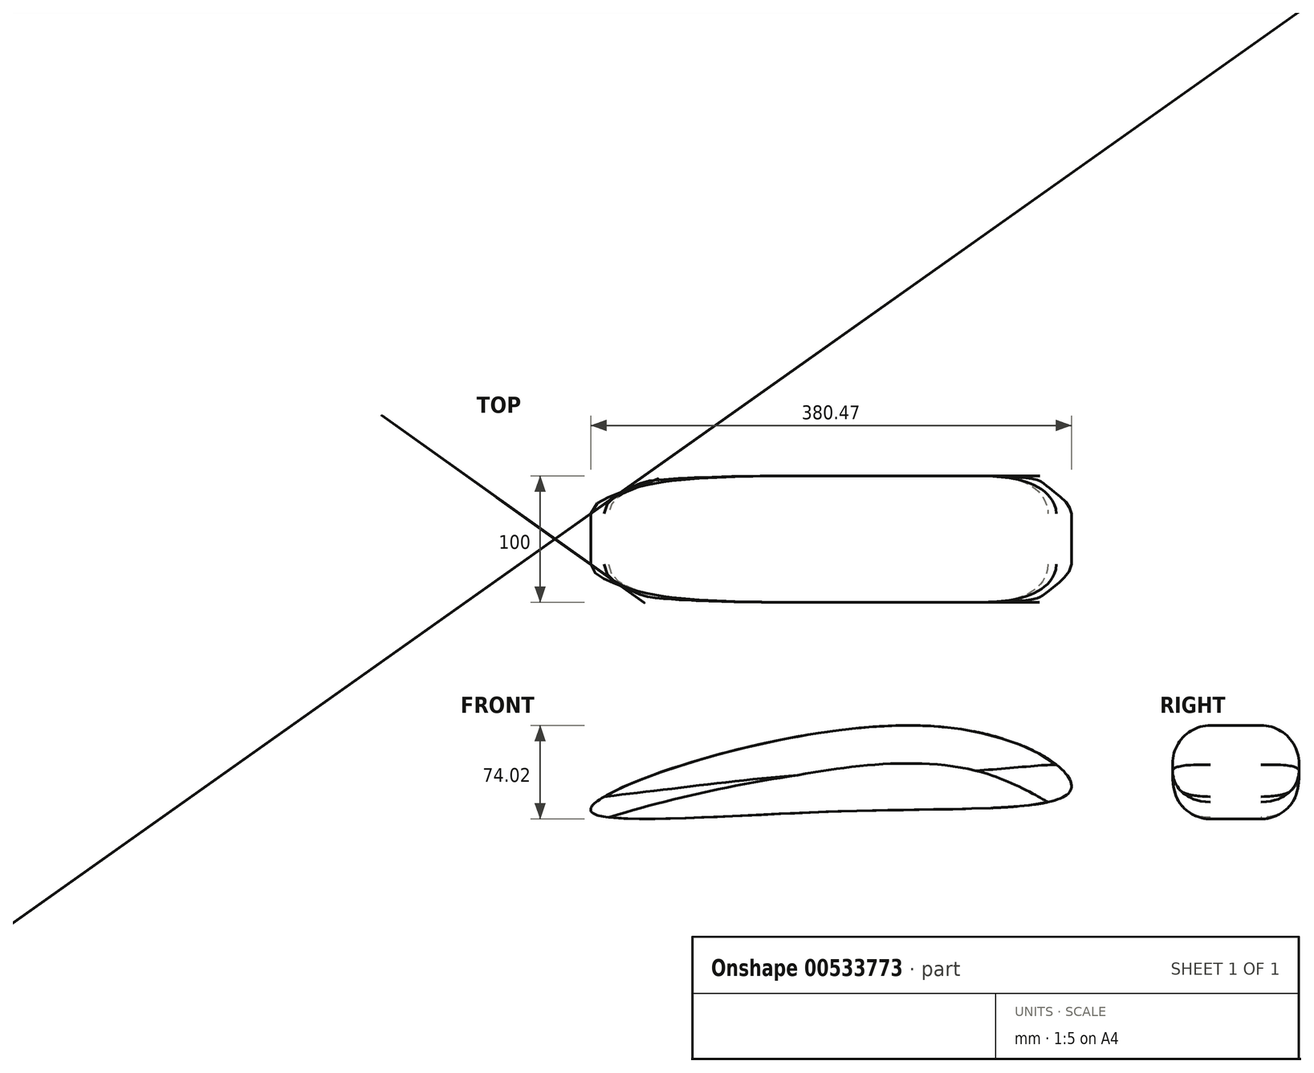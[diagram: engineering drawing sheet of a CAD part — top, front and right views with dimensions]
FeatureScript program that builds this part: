
annotation { "Feature Type Name" : "Feature", "Feature Type Description" : "" }
export const myFeature = defineFeature(function(context is Context, id is Id, definition is map)
    precondition{}
    {
        {
            var Q0;
            Q0=qCreatedBy(makeId("Front.planeOp"),FACE);
            var sketch = newSketch(context, id + "F0", { "sketchPlane" : qUnion([Q0])});
            skFitSpline(sketch, "E0.0.0", {"points": [v(113.35, 23.22) * mm, v(113.44, 23.66) * mm, v(113.5, 24.56) * mm, v(113.2, 25.94) * mm, v(112.62, 27.29) * mm, v(111.79, 28.58) * mm, v(110.78, 29.82) * mm, v(109.65, 31) * mm, v(108.43, 32.12) * mm, v(106.71, 33.54) * mm, v(104.45, 35.18) * mm, v(101.68, 36.95) * mm, v(99.37, 38.26) * mm, v(97.55, 39.22) * mm, v(96.2, 39.89) * mm, v(94.85, 40.52) * mm, v(93.51, 41.11) * mm, v(92.17, 41.68) * mm, v(90.82, 42.23) * mm, v(89.45, 42.77) * mm, v(87.6, 43.47) * mm, v(85.24, 44.34) * mm, v(82.34, 45.37) * mm, v(79.4, 46.38) * mm, v(76.43, 47.36) * mm, v(73.46, 48.29) * mm, v(70.5, 49.16) * mm, v(67.54, 49.97) * mm, v(64.6, 50.72) * mm, v(61.64, 51.42) * mm, v(58.66, 52.07) * mm, v(54.68, 52.9) * mm, v(49.65, 53.84) * mm, v(43.57, 54.8) * mm, v(37.48, 55.61) * mm, v(31.4, 56.27) * mm, v(25.3, 56.82) * mm, v(19.19, 57.28) * mm, v(11.02, 57.8) * mm, v(2.86, 58.15) * mm, v(-5.3, 58.39) * mm, v(-11.44, 58.5) * mm, v(-17.57, 58.56) * mm, v(-23.7, 58.55) * mm, v(-29.82, 58.49) * mm, v(-38, 58.32) * mm, v(-48.2, 57.99) * mm, v(-58.4, 57.48) * mm, v(-66.56, 56.97) * mm, v(-72.68, 56.54) * mm, v(-78.79, 56.06) * mm, v(-86.93, 55.36) * mm, v(-97.1, 54.37) * mm, v(-107.24, 53.24) * mm, v(-115.35, 52.25) * mm, v(-121.43, 51.47) * mm, v(-127.5, 50.65) * mm, v(-135.58, 49.5) * mm, v(-145.64, 48) * mm, v(-155.68, 46.37) * mm, v(-163.73, 45) * mm, v(-169.76, 43.94) * mm, v(-175.8, 42.85) * mm, v(-181.8, 41.74) * mm, v(-187.8, 40.6) * mm, v(-192.81, 39.62) * mm, v(-196.82, 38.82) * mm, v(-200.83, 38.02) * mm, v(-207.85, 36.6) * mm, v(-214.87, 35.12) * mm, v(-220.87, 33.83) * mm, v(-223.86, 33.18) * mm, v(-226.86, 32.52) * mm, v(-229.87, 31.85) * mm, v(-232.9, 31.17) * mm, v(-235.92, 30.5) * mm, v(-238.94, 29.8) * mm, v(-241.93, 29.11) * mm, v(-244.91, 28.42) * mm, v(-247.9, 27.71) * mm, v(-250.86, 27) * mm, v(-254.8, 26.03) * mm, v(-259.73, 24.78) * mm, v(-263.68, 23.75) * mm, v(-265.65, 23.22) * mm]});
            skFitSpline(sketch, "E0.0.1", {"points": [v(-265.65, 23.22) * mm, v(-263.64, 23.1) * mm, v(-259.61, 22.89) * mm, v(-253.56, 22.6) * mm, v(-247.58, 22.34) * mm, v(-241.63, 22.12) * mm, v(-235.63, 21.9) * mm, v(-229.58, 21.7) * mm, v(-223.53, 21.5) * mm, v(-217.48, 21.29) * mm, v(-212.44, 21.12) * mm, v(-208.4, 20.98) * mm, v(-205.38, 20.88) * mm, v(-202.36, 20.78) * mm, v(-199.38, 20.68) * mm, v(-196.47, 20.58) * mm, v(-193.64, 20.48) * mm, v(-190.86, 20.39) * mm, v(-187.22, 20.26) * mm, v(-183.62, 20.14) * mm, v(-179.94, 20.01) * mm, v(-177.12, 19.92) * mm, v(-174.23, 19.82) * mm, v(-171.27, 19.71) * mm, v(-168.76, 19.63) * mm, v(-166.74, 19.56) * mm, v(-164.73, 19.49) * mm, v(-162.2, 19.4) * mm, v(-158.17, 19.26) * mm, v(-153.13, 19.09) * mm, v(-147.08, 18.88) * mm, v(-142.04, 18.7) * mm, v(-138, 18.56) * mm, v(-134.98, 18.46) * mm, v(-131.96, 18.35) * mm, v(-128.93, 18.25) * mm, v(-125.9, 18.15) * mm, v(-122.95, 18.04) * mm, v(-120.08, 17.94) * mm, v(-117.3, 17.85) * mm, v(-114.6, 17.76) * mm, v(-111.07, 17.63) * mm, v(-107.59, 17.51) * mm, v(-104.02, 17.4) * mm, v(-101.27, 17.3) * mm, v(-98.44, 17.2) * mm, v(-95.51, 17.1) * mm, v(-93.01, 17.01) * mm, v(-91, 16.94) * mm, v(-88.98, 16.87) * mm, v(-86.46, 16.78) * mm, v(-82.42, 16.64) * mm, v(-77.38, 16.47) * mm, v(-71.33, 16.26) * mm, v(-63.27, 15.98) * mm, v(-53.18, 15.63) * mm, v(-41.08, 15.2) * mm, v(-28.98, 14.79) * mm, v(-16.88, 14.37) * mm, v(-4.78, 13.94) * mm, v(5.3, 13.6) * mm, v(13.37, 13.33) * mm, v(19.42, 13.14) * mm, v(25.47, 12.95) * mm, v(31.5, 12.78) * mm, v(36.53, 12.67) * mm, v(40.57, 12.6) * mm, v(43.6, 12.56) * mm, v(46.65, 12.52) * mm, v(49.68, 12.5) * mm, v(52.71, 12.47) * mm, v(55.72, 12.45) * mm, v(58.73, 12.44) * mm, v(61.73, 12.45) * mm, v(64.75, 12.48) * mm, v(67.78, 12.54) * mm, v(70.84, 12.64) * mm, v(73.92, 12.77) * mm, v(77, 12.91) * mm, v(80.04, 13.07) * mm, v(83.04, 13.21) * mm, v(85.98, 13.35) * mm, v(88.87, 13.5) * mm, v(91.76, 13.69) * mm, v(94.23, 13.95) * mm, v(96.25, 14.24) * mm, v(98.3, 14.6) * mm, v(100.9, 15.16) * mm, v(104.05, 16.07) * mm, v(106.61, 17.05) * mm, v(108.54, 18) * mm, v(109.9, 18.81) * mm, v(111.12, 19.74) * mm, v(112.16, 20.77) * mm, v(112.95, 21.94) * mm, v(113.25, 22.78) * mm, v(113.35, 23.22) * mm]});
            skFitSpline(sketch, "E1", {"points": [v(131.64, -49.78) * mm, v(21.58, 0) * mm, v(-248.36, -65.23) * mm, v(-46.7, -67.35) * mm, v(131.64, -49.78) * mm]});
            skLineSegment(sketch, "E2", {"start": v(-248.36, -65.23) * mm, "end": v(131.64, -49.78) * mm, "construction": true});
            skSolve(sketch);
        }
        {
            var Q0;
            Q0=makeQuery(id+"F0.imprint","IMPRINT",FACE,{"disambiguationData":[TD([[makeQuery(id+"F0.imprint","IMPRINT",EDGE,{"derivedFrom":sQuery(id+"F0.wireOp",EDGE,"E1")}),1.0]])]});
            extrude(context, id + "F1", {"entities" : qUnion([Q0]), "depth" : 100 * mm, "offsetDistance" : 25 * mm});
        }
        {
            var Q0;
            Q0=makeQuery(id+"F1.opExtrude","CAP_EDGE",EDGE,{"disambiguationData":[OSD([sQuery(id+"F0.wireOp",EDGE,"E1")])],"isStart":true});
            var Q1;
            Q1=makeQuery(id+"F1.opExtrude","CAP_EDGE",EDGE,{"disambiguationData":[OSD([sQuery(id+"F0.wireOp",EDGE,"E1")])],"isStart":false});
            fillet(context, id + "F2", {"entities" : qUnion([Q0, Q1]), "radius" : 30 * mm, "tangentPropagation" : true, "allowEdgeOverflow" : false});
        }
    });
